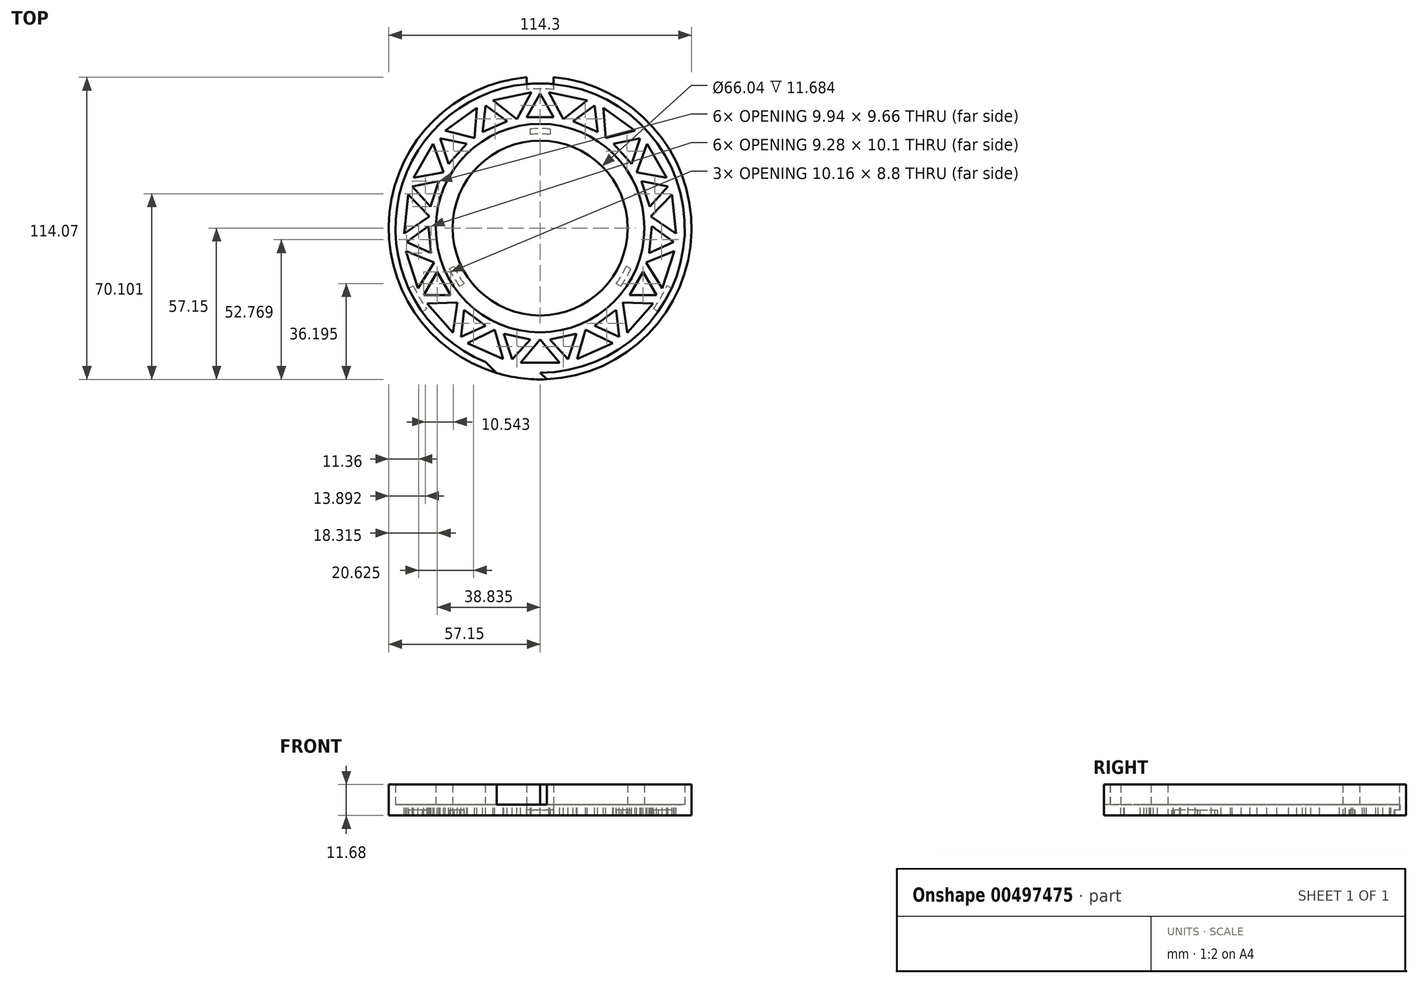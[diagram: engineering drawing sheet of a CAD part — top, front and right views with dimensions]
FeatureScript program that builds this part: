
annotation { "Feature Type Name" : "Feature", "Feature Type Description" : "" }
export const myFeature = defineFeature(function(context is Context, id is Id, definition is map)
    precondition{}
    {
        {
            var Q0;
            Q0=qCreatedBy(makeId("Top.planeOp"),FACE);
            var sketch = newSketch(context, id + "F0", { "sketchPlane" : qUnion([Q0])});
            skCircle(sketch, "E0", {"center": v(0, 0) * mm, "radius": 57.15 * mm});
            skSolve(sketch);
        }
        {
            var Q0;
            Q0=qCreatedBy(makeId("Top.planeOp"),FACE);
            var sketch = newSketch(context, id + "F1", { "sketchPlane" : qUnion([Q0])});
            skCircle(sketch, "E1", {"center": v(0, 0) * mm, "radius": 39.37 * mm});
            skArc(sketch, "E2", {"start": v(0, 54.61) * mm, "mid": v(-10.7, -53.55) * mm, "end": v(21, 50.41) * mm});
            skArc(sketch, "E3", {"start": v(0, 57.15) * mm, "mid": v(-13.88, -55.44) * mm, "end": v(26.92, 50.41) * mm});
            skCircle(sketch, "E4", {"center": v(0, 0) * mm, "radius": 33.02 * mm});
            skCircle(sketch, "E5", {"center": v(0, 0) * mm, "radius": 54.61 * mm});
            skCircle(sketch, "E6", {"center": v(0, 0) * mm, "radius": 57.15 * mm});
            skSolve(sketch);
        }
        {
            var Q0;
            Q0 = qSketchRegion(id + "F0", true);
            extrude(context, id + "F2", {"entities" : qUnion([Q0]), "depth" : 4.06 * mm});
        }
        {
            var Q0;
            Q0 = qSketchRegion(id + "F1", true);
            var Q1;
            Q1=makeQuery(id+"F1.imprint","IMPRINT",FACE,{"disambiguationData":[TD([[makeQuery(id+"F1.imprint","IMPRINT",EDGE,{"derivedFrom":sQuery(id+"F1.wireOp",EDGE,"E1")}),1.0]])]});
            extrude(context, id + "F3", {"entities" : qUnion([Q0, Q1]), "operationType" : NewBodyOperationType.ADD, "depth" : 11.68 * mm});
        }
        {
            var Q0;
            Q0=qCreatedBy(makeId("Top.planeOp"),FACE);
            var sketch = newSketch(context, id + "F4", { "sketchPlane" : qUnion([Q0])});
            skPoint(sketch, "E7", {"position": v(0, 0) * mm});
            skSolve(sketch);
        }
        {
            var Q0;
            Q0=sQuery(id+"F4.wireOp",VERTEX,"E7");
            var Q1;
            Q1=makeQuery(id+"F2.opExtrude","SWEPT_BODY",BODY,{"disambiguationData":[OSD([sQuery(id+"F0.wireOp",EDGE,"E0")])]});
            hole(context, id + "F5", {"style" : HoleStyle.SIMPLE, "endStyle" : HoleEndStyle.THROUGH, "oppositeDirection" : true, "holeDiameter" : 66.04 * mm, "isTappedThrough" : true, "tappedDepth" : 12.7 * mm, "tapClearance" : 3, "locations" : qUnion([Q0]), "scope" : qUnion([Q1])});
        }
        {
            var Q0;
            Q0=qCreatedBy(makeId("Top.planeOp"),FACE);
            var sketch = newSketch(context, id + "F6", { "sketchPlane" : qUnion([Q0])});
            skLineSegment(sketch, "E8", {"start": v(-5.08, 56.92) * mm, "end": v(-5.08, 54.37) * mm});
            skLineSegment(sketch, "E9", {"start": v(5.08, 54.37) * mm, "end": v(5.08, 56.92) * mm});
            skArc(sketch, "E10", {"start": v(-3.81, 32.8) * mm, "mid": v(0, 33.02) * mm, "end": v(3.81, 32.8) * mm});
            skArc(sketch, "E11", {"start": v(-3.8, 35.36) * mm, "mid": v(0, 35.56) * mm, "end": v(3.8, 35.36) * mm});
            skLineSegment(sketch, "E12", {"start": v(-3.81, 32.8) * mm, "end": v(-3.8, 35.36) * mm});
            skLineSegment(sketch, "E13", {"start": v(3.81, 32.8) * mm, "end": v(3.81, 35.36) * mm});
            skLineSegment(sketch, "E14", {"start": v(0, 0) * mm, "end": v(0, 76.2) * mm, "construction": true});
            skArc(sketch, "E15", {"start": v(-5.08, 56.92) * mm, "mid": v(0, 57.15) * mm, "end": v(5.08, 56.92) * mm});
            skArc(sketch, "E16", {"start": v(-5.08, 54.37) * mm, "mid": v(0, 54.61) * mm, "end": v(5.08, 54.37) * mm});
            skArc(sketch, "E17.1.1", {"start": v(-44.55, -31.59) * mm, "mid": v(-47.3, -27.3) * mm, "end": v(-49.63, -22.79) * mm});
            skArc(sketch, "E17.1.2", {"start": v(-26.5, -19.7) * mm, "mid": v(-28.6, -16.5) * mm, "end": v(-30.31, -13.1) * mm});
            skArc(sketch, "E17.1.3", {"start": v(-28.71, -20.98) * mm, "mid": v(-30.8, -17.78) * mm, "end": v(-32.52, -14.38) * mm});
            skLineSegment(sketch, "E17.1.4", {"start": v(0, 0) * mm, "end": v(-66, -38.1) * mm, "construction": true});
            skArc(sketch, "E17.1.5", {"start": v(-46.76, -32.86) * mm, "mid": v(-49.5, -28.57) * mm, "end": v(-51.84, -24.06) * mm});
            skArc(sketch, "E17.1.7", {"start": v(-44.55, -31.59) * mm, "mid": v(-47.3, -27.3) * mm, "end": v(-49.63, -22.79) * mm});
            skLineSegment(sketch, "E17.1.9", {"start": v(-30.31, -13.1) * mm, "end": v(-32.52, -14.38) * mm});
            skLineSegment(sketch, "E17.1.10", {"start": v(-26.5, -19.7) * mm, "end": v(-28.71, -20.98) * mm});
            skLineSegment(sketch, "E17.1.11", {"start": v(-49.63, -22.79) * mm, "end": v(-51.84, -24.06) * mm});
            skLineSegment(sketch, "E17.1.12", {"start": v(-46.76, -32.86) * mm, "end": v(-44.55, -31.59) * mm});
            skArc(sketch, "E17.2.1", {"start": v(49.63, -22.79) * mm, "mid": v(47.3, -27.3) * mm, "end": v(44.55, -31.59) * mm});
            skArc(sketch, "E17.2.2", {"start": v(30.31, -13.1) * mm, "mid": v(28.6, -16.5) * mm, "end": v(26.5, -19.7) * mm});
            skArc(sketch, "E17.2.3", {"start": v(32.52, -14.38) * mm, "mid": v(30.8, -17.78) * mm, "end": v(28.71, -20.98) * mm});
            skLineSegment(sketch, "E17.2.4", {"start": v(0, 0) * mm, "end": v(66, -38.1) * mm, "construction": true});
            skArc(sketch, "E17.2.5", {"start": v(51.84, -24.06) * mm, "mid": v(49.5, -28.58) * mm, "end": v(46.76, -32.86) * mm});
            skArc(sketch, "E17.2.7", {"start": v(49.63, -22.79) * mm, "mid": v(47.3, -27.3) * mm, "end": v(44.55, -31.59) * mm});
            skLineSegment(sketch, "E17.2.9", {"start": v(26.5, -19.7) * mm, "end": v(28.71, -20.98) * mm});
            skLineSegment(sketch, "E17.2.10", {"start": v(30.31, -13.1) * mm, "end": v(32.52, -14.38) * mm});
            skLineSegment(sketch, "E17.2.11", {"start": v(44.55, -31.59) * mm, "end": v(46.76, -32.86) * mm});
            skLineSegment(sketch, "E17.2.12", {"start": v(51.84, -24.06) * mm, "end": v(49.63, -22.79) * mm});
            skSolve(sketch);
        }
        {
            var Q0;
            Q0=makeQuery(id+"F6.imprint","IMPRINT",FACE,{"disambiguationData":[TD([[makeQuery(id+"F6.imprint","IMPRINT",EDGE,{"derivedFrom":sQuery(id+"F6.wireOp",EDGE,"E17.1.5")}),-1.0]])]});
            var Q1;
            Q1=makeQuery(id+"F6.imprint","IMPRINT",FACE,{"disambiguationData":[TD([[makeQuery(id+"F6.imprint","IMPRINT",EDGE,{"derivedFrom":sQuery(id+"F6.wireOp",EDGE,"E17.1.2")}),1.0]])]});
            var Q2;
            Q2=makeQuery(id+"F6.imprint","IMPRINT",FACE,{"disambiguationData":[TD([[makeQuery(id+"F6.imprint","IMPRINT",EDGE,{"derivedFrom":sQuery(id+"F6.wireOp",EDGE,"E17.2.2")}),1.0]])]});
            var Q3;
            Q3=makeQuery(id+"F6.imprint","IMPRINT",FACE,{"disambiguationData":[TD([[makeQuery(id+"F6.imprint","IMPRINT",EDGE,{"derivedFrom":sQuery(id+"F6.wireOp",EDGE,"E17.2.5")}),-1.0]])]});
            var Q4;
            Q4=makeQuery(id+"F6.imprint","IMPRINT",FACE,{"disambiguationData":[TD([[makeQuery(id+"F6.imprint","IMPRINT",EDGE,{"derivedFrom":sQuery(id+"F6.wireOp",EDGE,"E10")}),1.0]])]});
            var Q5;
            Q5=makeQuery(id+"F6.imprint","IMPRINT",FACE,{"disambiguationData":[TD([[makeQuery(id+"F6.imprint","IMPRINT",EDGE,{"derivedFrom":sQuery(id+"F6.wireOp",EDGE,"E8")}),1.0]])]});
            extrude(context, id + "F7", {"entities" : qUnion([Q0, Q1, Q2, Q3, Q4, Q5]), "operationType" : NewBodyOperationType.REMOVE, "endBound" : BoundingType.THROUGH_ALL, "depth" : 25.4 * mm});
        }
        {
            var Q0;
            Q0=makeQuery(id+"F2.opExtrude","CAP_FACE",FACE,{"disambiguationData":[OSD([sQuery(id+"F0.wireOp",EDGE,"E0")])],"isStart":true});
            var sketch = newSketch(context, id + "F8", { "sketchPlane" : qUnion([Q0])});
            skPoint(sketch, "E18.center", {"position": v(0, 0) * mm});
            skArc(sketch, "E19", {"start": v(-3.8, -35.36) * mm, "mid": v(0, -35.56) * mm, "end": v(3.8, -35.36) * mm});
            skArc(sketch, "E20", {"start": v(-3.8, -37.39) * mm, "mid": v(0, -37.58) * mm, "end": v(3.8, -37.39) * mm});
            skLineSegment(sketch, "E21", {"start": v(3.81, -37.39) * mm, "end": v(3.81, -35.36) * mm});
            skLineSegment(sketch, "E22", {"start": v(-3.8, -37.39) * mm, "end": v(-3.8, -35.36) * mm});
            skArc(sketch, "E23", {"start": v(-5.08, -54.37) * mm, "mid": v(0, -54.61) * mm, "end": v(5.08, -54.37) * mm});
            skArc(sketch, "E24", {"start": v(-5.08, -52.34) * mm, "mid": v(0, -52.59) * mm, "end": v(5.08, -52.34) * mm});
            skLineSegment(sketch, "E25", {"start": v(-5.08, -54.37) * mm, "end": v(-5.08, -52.34) * mm});
            skLineSegment(sketch, "E26", {"start": v(5.08, -54.37) * mm, "end": v(5.08, -52.34) * mm});
            skArc(sketch, "E27.1.0", {"start": v(34.28, 15.4) * mm, "mid": v(32.55, 18.8) * mm, "end": v(30.47, 22) * mm});
            skArc(sketch, "E27.1.1", {"start": v(47.87, 21.77) * mm, "mid": v(45.54, 26.3) * mm, "end": v(42.79, 30.57) * mm});
            skArc(sketch, "E27.1.2", {"start": v(49.63, 22.79) * mm, "mid": v(47.3, 27.3) * mm, "end": v(44.55, 31.59) * mm});
            skArc(sketch, "E27.1.3", {"start": v(32.52, 14.38) * mm, "mid": v(30.8, 17.78) * mm, "end": v(28.71, 20.98) * mm});
            skLineSegment(sketch, "E27.1.4", {"start": v(34.28, 15.4) * mm, "end": v(32.52, 14.38) * mm});
            skLineSegment(sketch, "E27.1.5", {"start": v(49.63, 22.79) * mm, "end": v(47.87, 21.77) * mm});
            skLineSegment(sketch, "E27.1.6", {"start": v(30.47, 22) * mm, "end": v(28.71, 20.98) * mm});
            skLineSegment(sketch, "E27.1.7", {"start": v(44.55, 31.59) * mm, "end": v(42.79, 30.57) * mm});
            skArc(sketch, "E27.2.0", {"start": v(-30.47, 22) * mm, "mid": v(-32.55, 18.8) * mm, "end": v(-34.28, 15.4) * mm});
            skArc(sketch, "E27.2.1", {"start": v(-42.79, 30.57) * mm, "mid": v(-45.54, 26.3) * mm, "end": v(-47.87, 21.77) * mm});
            skArc(sketch, "E27.2.2", {"start": v(-44.55, 31.59) * mm, "mid": v(-47.3, 27.3) * mm, "end": v(-49.63, 22.79) * mm});
            skArc(sketch, "E27.2.3", {"start": v(-28.71, 20.98) * mm, "mid": v(-30.8, 17.78) * mm, "end": v(-32.52, 14.38) * mm});
            skLineSegment(sketch, "E27.2.4", {"start": v(-30.47, 22) * mm, "end": v(-28.71, 20.98) * mm});
            skLineSegment(sketch, "E27.2.5", {"start": v(-44.55, 31.59) * mm, "end": v(-42.79, 30.57) * mm});
            skLineSegment(sketch, "E27.2.6", {"start": v(-34.28, 15.4) * mm, "end": v(-32.52, 14.38) * mm});
            skLineSegment(sketch, "E27.2.7", {"start": v(-49.63, 22.79) * mm, "end": v(-47.87, 21.77) * mm});
            skSolve(sketch);
        }
        {
            var Q0;
            Q0 = qSketchRegion(id + "F8", true);
            extrude(context, id + "F9", {"entities" : qUnion([Q0]), "operationType" : NewBodyOperationType.REMOVE, "oppositeDirection" : true, "depth" : 2.03 * mm});
        }
        {
            var Q0;
            {var subQ0=sQuery(id+"F1.wireOp",EDGE,"E6");var subQ1=sQuery(id+"F1.wireOp",EDGE,"E5");Q0=makeQuery(id+"F7.boolean.opBoolean","SPLIT",FACE,{"disambiguationData":[TD([makeQuery(id+"F7.opExtrude","SWEPT_FACE",FACE,{"disambiguationData":[OSD([sQuery(id+"F6.wireOp",EDGE,"E17.1.12")])]})])],"derivedFrom":makeQuery(id+"F3.opExtrude","CAP_FACE",FACE,{"disambiguationData":[OSD([subQ1,subQ0])],"isStart":false})});}
            var sketch = newSketch(context, id + "F10", { "sketchPlane" : qUnion([Q0])});
            skLineSegment(sketch, "E28", {"start": v(0, -54.6) * mm, "end": v(2.49, -57.1) * mm});
            skLineSegment(sketch, "E29", {"start": v(-20.57, -50.59) * mm, "end": v(-16.42, -54.74) * mm});
            skSolve(sketch);
        }
        {
            var Q0;
            {var subQ0=sQuery(id+"F10.wireOp",EDGE,"E28");Q0=makeQuery(id+"F10.imprint","IMPRINT",FACE,{"disambiguationData":[TD([[makeQuery(id+"F10.imprint","IMPRINT",EDGE,{"derivedFrom":subQ0}),-1.0]])]});}
            extrude(context, id + "F11", {"entities" : qUnion([Q0]), "operationType" : NewBodyOperationType.REMOVE, "oppositeDirection" : true, "depth" : 7.62 * mm});
        }
        {
            var Q0;
            {var subQ0=sQuery(id+"F1.wireOp",EDGE,"E5");Q0=makeQuery(id+"F11.boolean.opBoolean","MERGE",FACE,{"derivedFrom":[makeQuery(id+"F3.boolean.opBoolean","SPLIT",FACE,{"disambiguationData":[TD([makeQuery(id+"F3.opExtrude","SWEPT_FACE",FACE,{"disambiguationData":[OSD([sQuery(id+"F1.wireOp",EDGE,"E1")])]})])],"derivedFrom":makeQuery(id+"F2.opExtrude","CAP_FACE",FACE,{"disambiguationData":[OSD([sQuery(id+"F0.wireOp",EDGE,"E0")])],"isStart":false})}),makeQuery(id+"F11.opExtrude","CAP_FACE",FACE,{"disambiguationData":[OSD([subQ0,sQuery(id+"F1.wireOp",EDGE,"E6"),sQuery(id+"F10.wireOp",EDGE,"E28"),sQuery(id+"F10.wireOp",EDGE,"E29")])],"isStart":false})]});}
            var sketch = newSketch(context, id + "F12", { "sketchPlane" : qUnion([Q0])});
            skLineSegment(sketch, "E30", {"start": v(-5.08, 41.91) * mm, "end": v(0, 50.7) * mm});
            skLineSegment(sketch, "E31", {"start": v(0, 50.7) * mm, "end": v(5.08, 41.91) * mm});
            skLineSegment(sketch, "E32", {"start": v(5.08, 41.91) * mm, "end": v(-5.08, 41.91) * mm});
            skLineSegment(sketch, "E33.1.0", {"start": v(-12.4, 40.35) * mm, "end": v(-21.69, 36.22) * mm});
            skLineSegment(sketch, "E33.1.1", {"start": v(-20.63, 46.32) * mm, "end": v(-12.4, 40.35) * mm});
            skLineSegment(sketch, "E33.1.2", {"start": v(-21.69, 36.22) * mm, "end": v(-20.63, 46.32) * mm});
            skLineSegment(sketch, "E33.2.0", {"start": v(-27.75, 31.82) * mm, "end": v(-34.54, 24.27) * mm});
            skLineSegment(sketch, "E33.2.1", {"start": v(-37.68, 33.93) * mm, "end": v(-27.75, 31.82) * mm});
            skLineSegment(sketch, "E33.2.2", {"start": v(-34.54, 24.27) * mm, "end": v(-37.68, 33.93) * mm});
            skLineSegment(sketch, "E33.3.0", {"start": v(-38.29, 17.78) * mm, "end": v(-41.43, 8.12) * mm});
            skLineSegment(sketch, "E33.3.1", {"start": v(-48.23, 15.67) * mm, "end": v(-38.29, 17.78) * mm});
            skLineSegment(sketch, "E33.3.2", {"start": v(-41.43, 8.12) * mm, "end": v(-48.23, 15.67) * mm});
            skLineSegment(sketch, "E33.4.0", {"start": v(-42.21, 0.67) * mm, "end": v(-41.15, -9.43) * mm});
            skLineSegment(sketch, "E33.4.1", {"start": v(-50.43, -5.3) * mm, "end": v(-42.21, 0.67) * mm});
            skLineSegment(sketch, "E33.4.2", {"start": v(-41.15, -9.43) * mm, "end": v(-50.43, -5.3) * mm});
            skLineSegment(sketch, "E33.5.0", {"start": v(-38.84, -16.56) * mm, "end": v(-33.76, -25.35) * mm});
            skLineSegment(sketch, "E33.5.1", {"start": v(-43.92, -25.35) * mm, "end": v(-38.84, -16.56) * mm});
            skLineSegment(sketch, "E33.5.2", {"start": v(-33.76, -25.35) * mm, "end": v(-43.92, -25.35) * mm});
            skLineSegment(sketch, "E33.6.0", {"start": v(-28.74, -30.92) * mm, "end": v(-20.52, -36.9) * mm});
            skLineSegment(sketch, "E33.6.1", {"start": v(-29.8, -41.02) * mm, "end": v(-28.74, -30.92) * mm});
            skLineSegment(sketch, "E33.6.2", {"start": v(-20.52, -36.9) * mm, "end": v(-29.8, -41.02) * mm});
            skLineSegment(sketch, "E33.7.0", {"start": v(-13.68, -39.94) * mm, "end": v(-3.74, -42.05) * mm});
            skLineSegment(sketch, "E33.7.1", {"start": v(-10.54, -49.6) * mm, "end": v(-13.68, -39.94) * mm});
            skLineSegment(sketch, "E33.7.2", {"start": v(-3.74, -42.05) * mm, "end": v(-10.54, -49.6) * mm});
            skLineSegment(sketch, "E33.8.0", {"start": v(3.74, -42.05) * mm, "end": v(13.68, -39.94) * mm});
            skLineSegment(sketch, "E33.8.1", {"start": v(10.54, -49.6) * mm, "end": v(3.74, -42.05) * mm});
            skLineSegment(sketch, "E33.8.2", {"start": v(13.68, -39.94) * mm, "end": v(10.54, -49.6) * mm});
            skLineSegment(sketch, "E33.9.0", {"start": v(20.52, -36.9) * mm, "end": v(28.74, -30.92) * mm});
            skLineSegment(sketch, "E33.9.1", {"start": v(29.8, -41.02) * mm, "end": v(20.52, -36.9) * mm});
            skLineSegment(sketch, "E33.9.2", {"start": v(28.74, -30.92) * mm, "end": v(29.8, -41.02) * mm});
            skLineSegment(sketch, "E33.10.0", {"start": v(33.76, -25.35) * mm, "end": v(38.84, -16.56) * mm});
            skLineSegment(sketch, "E33.10.1", {"start": v(43.92, -25.35) * mm, "end": v(33.76, -25.35) * mm});
            skLineSegment(sketch, "E33.10.2", {"start": v(38.84, -16.56) * mm, "end": v(43.92, -25.35) * mm});
            skLineSegment(sketch, "E33.11.0", {"start": v(41.15, -9.43) * mm, "end": v(42.21, 0.67) * mm});
            skLineSegment(sketch, "E33.11.1", {"start": v(50.43, -5.3) * mm, "end": v(41.15, -9.43) * mm});
            skLineSegment(sketch, "E33.11.2", {"start": v(42.21, 0.67) * mm, "end": v(50.43, -5.3) * mm});
            skLineSegment(sketch, "E33.12.0", {"start": v(41.43, 8.12) * mm, "end": v(38.29, 17.78) * mm});
            skLineSegment(sketch, "E33.12.1", {"start": v(48.23, 15.67) * mm, "end": v(41.43, 8.12) * mm});
            skLineSegment(sketch, "E33.12.2", {"start": v(38.29, 17.78) * mm, "end": v(48.23, 15.67) * mm});
            skLineSegment(sketch, "E33.13.0", {"start": v(34.54, 24.27) * mm, "end": v(27.75, 31.82) * mm});
            skLineSegment(sketch, "E33.13.1", {"start": v(37.68, 33.93) * mm, "end": v(34.54, 24.27) * mm});
            skLineSegment(sketch, "E33.13.2", {"start": v(27.75, 31.82) * mm, "end": v(37.68, 33.93) * mm});
            skLineSegment(sketch, "E33.14.0", {"start": v(21.69, 36.22) * mm, "end": v(12.4, 40.35) * mm});
            skLineSegment(sketch, "E33.14.1", {"start": v(20.63, 46.32) * mm, "end": v(21.69, 36.22) * mm});
            skLineSegment(sketch, "E33.14.2", {"start": v(12.4, 40.35) * mm, "end": v(20.63, 46.32) * mm});
            skPoint(sketch, "E33.center", {"position": v(0, 0) * mm});
            skLineSegment(sketch, "E34", {"start": v(0, -42.05) * mm, "end": v(-7.37, -50.84) * mm});
            skLineSegment(sketch, "E35", {"start": v(-7.37, -50.84) * mm, "end": v(7.37, -50.84) * mm});
            skLineSegment(sketch, "E36", {"start": v(7.37, -50.84) * mm, "end": v(0, -42.05) * mm});
            skLineSegment(sketch, "E37", {"start": v(3.74, -42.05) * mm, "end": v(-3.74, -42.05) * mm, "construction": true});
            skPoint(sketch, "E38", {"position": v(0, -50.84) * mm});
            skLineSegment(sketch, "E39.1.0", {"start": v(27.41, -43.44) * mm, "end": v(17.1, -38.41) * mm});
            skLineSegment(sketch, "E39.1.1", {"start": v(13.94, -49.44) * mm, "end": v(27.41, -43.44) * mm});
            skLineSegment(sketch, "E39.1.2", {"start": v(17.1, -38.41) * mm, "end": v(13.94, -49.44) * mm});
            skLineSegment(sketch, "E39.2.0", {"start": v(42.71, -28.54) * mm, "end": v(31.25, -28.14) * mm});
            skLineSegment(sketch, "E39.2.1", {"start": v(32.85, -39.5) * mm, "end": v(42.71, -28.54) * mm});
            skLineSegment(sketch, "E39.2.2", {"start": v(31.25, -28.14) * mm, "end": v(32.85, -39.5) * mm});
            skLineSegment(sketch, "E39.3.0", {"start": v(50.63, -8.7) * mm, "end": v(40, -13) * mm});
            skLineSegment(sketch, "E39.3.1", {"start": v(46.07, -22.72) * mm, "end": v(50.63, -8.7) * mm});
            skLineSegment(sketch, "E39.3.2", {"start": v(40, -13) * mm, "end": v(46.07, -22.72) * mm});
            skLineSegment(sketch, "E39.4.0", {"start": v(49.79, 12.65) * mm, "end": v(41.82, 4.4) * mm});
            skLineSegment(sketch, "E39.4.1", {"start": v(51.33, -2.02) * mm, "end": v(49.79, 12.65) * mm});
            skLineSegment(sketch, "E39.4.2", {"start": v(41.82, 4.4) * mm, "end": v(51.33, -2.02) * mm});
            skLineSegment(sketch, "E39.5.0", {"start": v(40.34, 31.8) * mm, "end": v(36.42, 21.03) * mm});
            skLineSegment(sketch, "E39.5.1", {"start": v(47.71, 19.03) * mm, "end": v(40.34, 31.8) * mm});
            skLineSegment(sketch, "E39.5.2", {"start": v(36.42, 21.03) * mm, "end": v(47.71, 19.03) * mm});
            skLineSegment(sketch, "E39.6.0", {"start": v(23.92, 45.46) * mm, "end": v(24.72, 34.02) * mm});
            skLineSegment(sketch, "E39.6.1", {"start": v(35.85, 36.8) * mm, "end": v(23.92, 45.46) * mm});
            skLineSegment(sketch, "E39.6.2", {"start": v(24.72, 34.02) * mm, "end": v(35.85, 36.8) * mm});
            skLineSegment(sketch, "E39.7.0", {"start": v(3.36, 51.26) * mm, "end": v(8.74, 41.13) * mm});
            skLineSegment(sketch, "E39.7.1", {"start": v(17.78, 48.2) * mm, "end": v(3.36, 51.26) * mm});
            skLineSegment(sketch, "E39.7.2", {"start": v(8.74, 41.13) * mm, "end": v(17.78, 48.2) * mm});
            skLineSegment(sketch, "E39.8.0", {"start": v(-17.78, 48.2) * mm, "end": v(-8.74, 41.13) * mm});
            skLineSegment(sketch, "E39.8.1", {"start": v(-3.36, 51.26) * mm, "end": v(-17.78, 48.2) * mm});
            skLineSegment(sketch, "E39.8.2", {"start": v(-8.74, 41.13) * mm, "end": v(-3.36, 51.26) * mm});
            skLineSegment(sketch, "E39.9.0", {"start": v(-35.85, 36.8) * mm, "end": v(-24.72, 34.02) * mm});
            skLineSegment(sketch, "E39.9.1", {"start": v(-23.92, 45.46) * mm, "end": v(-35.85, 36.8) * mm});
            skLineSegment(sketch, "E39.9.2", {"start": v(-24.72, 34.02) * mm, "end": v(-23.92, 45.46) * mm});
            skLineSegment(sketch, "E39.10.0", {"start": v(-47.71, 19.03) * mm, "end": v(-36.42, 21.03) * mm});
            skLineSegment(sketch, "E39.10.1", {"start": v(-40.34, 31.8) * mm, "end": v(-47.71, 19.03) * mm});
            skLineSegment(sketch, "E39.10.2", {"start": v(-36.42, 21.03) * mm, "end": v(-40.34, 31.8) * mm});
            skLineSegment(sketch, "E39.11.0", {"start": v(-51.33, -2.02) * mm, "end": v(-41.82, 4.4) * mm});
            skLineSegment(sketch, "E39.11.1", {"start": v(-49.79, 12.65) * mm, "end": v(-51.33, -2.02) * mm});
            skLineSegment(sketch, "E39.11.2", {"start": v(-41.82, 4.4) * mm, "end": v(-49.79, 12.65) * mm});
            skLineSegment(sketch, "E39.12.0", {"start": v(-46.07, -22.72) * mm, "end": v(-40, -13) * mm});
            skLineSegment(sketch, "E39.12.1", {"start": v(-50.63, -8.7) * mm, "end": v(-46.07, -22.72) * mm});
            skLineSegment(sketch, "E39.12.2", {"start": v(-40, -13) * mm, "end": v(-50.63, -8.7) * mm});
            skLineSegment(sketch, "E39.13.0", {"start": v(-32.85, -39.5) * mm, "end": v(-31.25, -28.14) * mm});
            skLineSegment(sketch, "E39.13.1", {"start": v(-42.71, -28.54) * mm, "end": v(-32.85, -39.5) * mm});
            skLineSegment(sketch, "E39.13.2", {"start": v(-31.25, -28.14) * mm, "end": v(-42.71, -28.54) * mm});
            skLineSegment(sketch, "E39.14.0", {"start": v(-13.94, -49.44) * mm, "end": v(-17.1, -38.41) * mm});
            skLineSegment(sketch, "E39.14.1", {"start": v(-27.41, -43.44) * mm, "end": v(-13.94, -49.44) * mm});
            skLineSegment(sketch, "E39.14.2", {"start": v(-17.1, -38.41) * mm, "end": v(-27.41, -43.44) * mm});
            skSolve(sketch);
        }
        {
            var Q0;
            Q0 = qSketchRegion(id + "F12", true);
            extrude(context, id + "F13", {"entities" : qUnion([Q0]), "operationType" : NewBodyOperationType.REMOVE, "endBound" : BoundingType.THROUGH_ALL, "oppositeDirection" : true, "depth" : 25.4 * mm});
        }
    });
